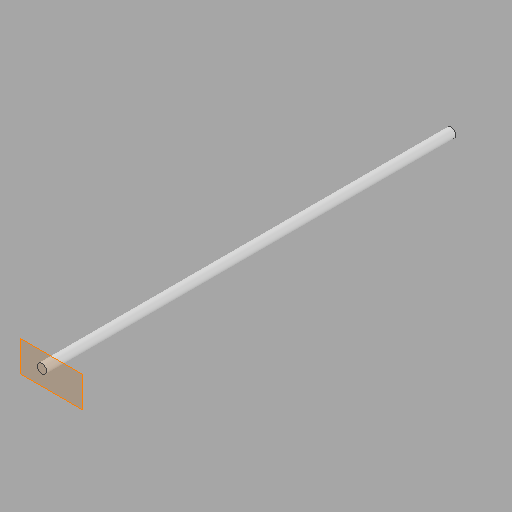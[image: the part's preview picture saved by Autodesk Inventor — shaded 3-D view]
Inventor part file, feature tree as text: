
AUTODESK INVENTOR PART (.ipt)
format: ipt  version: 2025 (Build 290162000, 162)  size: 80,384 bytes
history: native  units: in
note: dims shown in document units (in); Inventor stores cm internally (conversion verified against a paired STEP export)
features: other x3, sketch x1, plane x1
ambient origin geometry x8: Origin, YZ Plane, XZ Plane, XY Plane, X Axis, Y Axis, Z Axis, Center Point
bodies: Solid1 (feature_tree)
feature tree (5):
  other  "Boom.ipt"
  other  "Solid1::Boom.ipt"
  other  "TaggingFeature1"
  sketch  "Sketch1"  dims[d0=0.3937in]
  plane  "Work Plane1"
